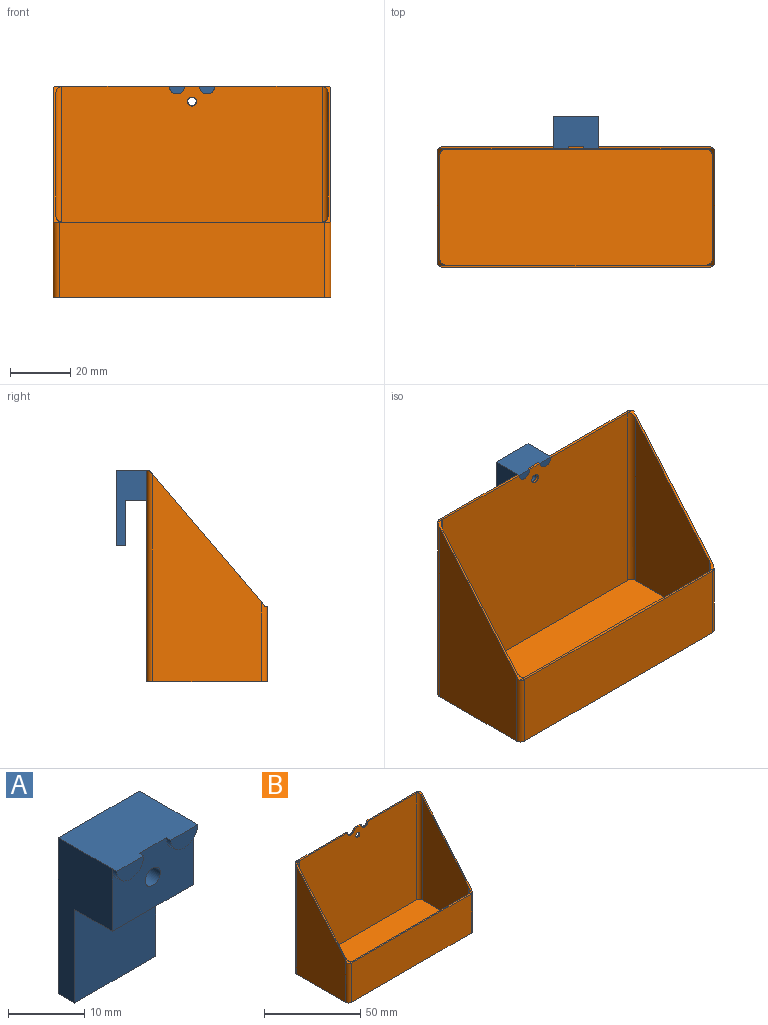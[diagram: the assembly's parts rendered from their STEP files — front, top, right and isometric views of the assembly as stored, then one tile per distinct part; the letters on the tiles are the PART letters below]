
ASSEMBLY  parts=2 mates=1
PART A: 13 faces, bbox 15x10.8x25 mm
  f0: plane 15x10mm, normal (0,-1,0), area 124.2mm2, adj f1,f3,f4,f6,f8,f9,f11
  f1: plane 25x10mm, normal (-1,0,0), area 145mm2, adj f0,f2,f4,f5,f6,f7
  f2: plane 15x3mm, normal (0,0,-1), area 45mm2, adj f1,f3,f5,f7
  f3: plane 25x10mm, normal (1,0,0), area 145mm2, adj f0,f2,f4,f5,f6,f7
  f4: plane 15x10.8mm, normal (0,0,1), area 158mm2, adj f0,f1,f3,f5,f9,f10,f11,f12
  f5: plane 25x15mm, normal (0,1,0), area 368.8mm2, adj f1,f2,f3,f4,f8
  f6: plane 15x7mm, normal (0,0,-1), area 105mm2, adj f0,f1,f3,f7
  f7: plane 15x15mm, normal (0,-1,0), area 225mm2, adj f1,f2,f3,f6
  f8: cylinder r=1.4mm len=10mm, axis (0,-1,0), area 88mm2, adj f0,f5
  f9: cylinder r=2.5mm len=5mm, axis (0,1,0), area 6.3mm2, adj f0,f4,f10
  f10: plane 5x2.5mm, normal (0,-1,0), area 9.8mm2, adj f4,f9
  f11: cylinder r=2.5mm len=5mm, axis (0,1,0), area 6.3mm2, adj f0,f4,f12
  f12: plane 5x2.5mm, normal (0,-1,0), area 9.8mm2, adj f4,f11
PART B: 27 faces, bbox 92x40x70 mm
  f0: plane 38.1x0.8mm, normal (0,0,1), area 30.1mm2, adj f6,f8,f15,f22,f26
  f1: plane 5x0.8mm, normal (0,0,1), area 4mm2, adj f6,f8,f25,f26
  f2: plane 38.1x0.8mm, normal (0,0,1), area 30.1mm2, adj f6,f8,f13,f23,f25
  f3: plane 88x25mm, normal (0,-1,0), area 2200mm2, adj f7,f14,f20,f21
  f4: plane 68.59x36mm, normal (1,0,0), area 1710mm2, adj f7,f15,f21,f22
  f5: plane 68.59x36mm, normal (-1,0,0), area 1710mm2, adj f7,f13,f20,f23
  f6: plane 88x70mm, normal (0,1,0), area 6133.3mm2, adj f0,f1,f2,f7,f22,f23,f24,f25
  f7: plane 92x40mm, normal (0,0,-1), area 3676.6mm2, adj f3,f4,f5,f6,f20,f21,f22,f23
  f8: plane 86.4x68mm, normal (0,-1,0), area 5848.5mm2, adj f0,f1,f2,f12,f16,f19,f24,f25
  f9: plane 65.66x34.4mm, normal (1,0,0), area 1565.2mm2, adj f12,f13,f16,f17
  f10: plane 86.4x23mm, normal (0,1,0), area 1987.2mm2, adj f12,f14,f17,f18
  f11: plane 65.66x34.4mm, normal (-1,0,0), area 1565.2mm2, adj f12,f15,f18,f19
  f12: plane 90.4x38.4mm, normal (0,0,1), area 3467.9mm2, adj f8,f9,f10,f11,f16,f17,f18,f19
  f13: plane 45x38.4mm, normal (0,-0.76,0.65), area 49.5mm2, adj f2,f5,f9,f14,f16,f17,f20,f23
  f14: plane 91.2x0.8mm, normal (0,0,1), area 72.2mm2, adj f3,f10,f13,f15,f20,f21
  f15: plane 45x38.4mm, normal (0,-0.76,0.65), area 49.5mm2, adj f0,f4,f11,f14,f18,f19,f21,f22
  f16: cylinder r=2mm len=68mm, axis (0,0,1), area 211mm2, adj f8,f9,f12,f13
  f17: cylinder r=2mm len=25.34mm, axis (0,0,-1), area 74.9mm2, adj f9,f10,f12,f13
  f18: cylinder r=2mm len=25.34mm, axis (0,0,1), area 74.9mm2, adj f10,f11,f12,f15
  f19: cylinder r=2mm len=68mm, axis (0,0,-1), area 211mm2, adj f8,f11,f12,f15
  f20: cylinder r=2mm len=26.41mm, axis (0,0,1), area 79.4mm2, adj f3,f5,f7,f13,f14
  f21: cylinder r=2mm len=26.41mm, axis (0,0,-1), area 79.4mm2, adj f3,f4,f7,f14,f15
  f22: cylinder r=2mm len=70mm, axis (0,0,1), area 219mm2, adj f0,f4,f6,f7,f15
  f23: cylinder r=2mm len=70mm, axis (0,0,-1), area 219mm2, adj f2,f5,f6,f7,f13
  f24: cylinder r=1.5mm len=3mm, axis (0,1,0), area 7.5mm2, adj f6,f8
  f25: cylinder r=2.5mm len=5mm, axis (0,1,0), area 6.3mm2, adj f1,f2,f6,f8
  f26: cylinder r=2.5mm len=5mm, axis (0,1,0), area 6.3mm2, adj f0,f1,f6,f8
PLACE A t=(-1.03,61.4,39.39)mm
PLACE B t=(-39.53,11.4,-5.61)mm
MATE fastened A.f8 <-> B.f24  axis (0,-1,0) through (6.47,51.4,59.39)mm
